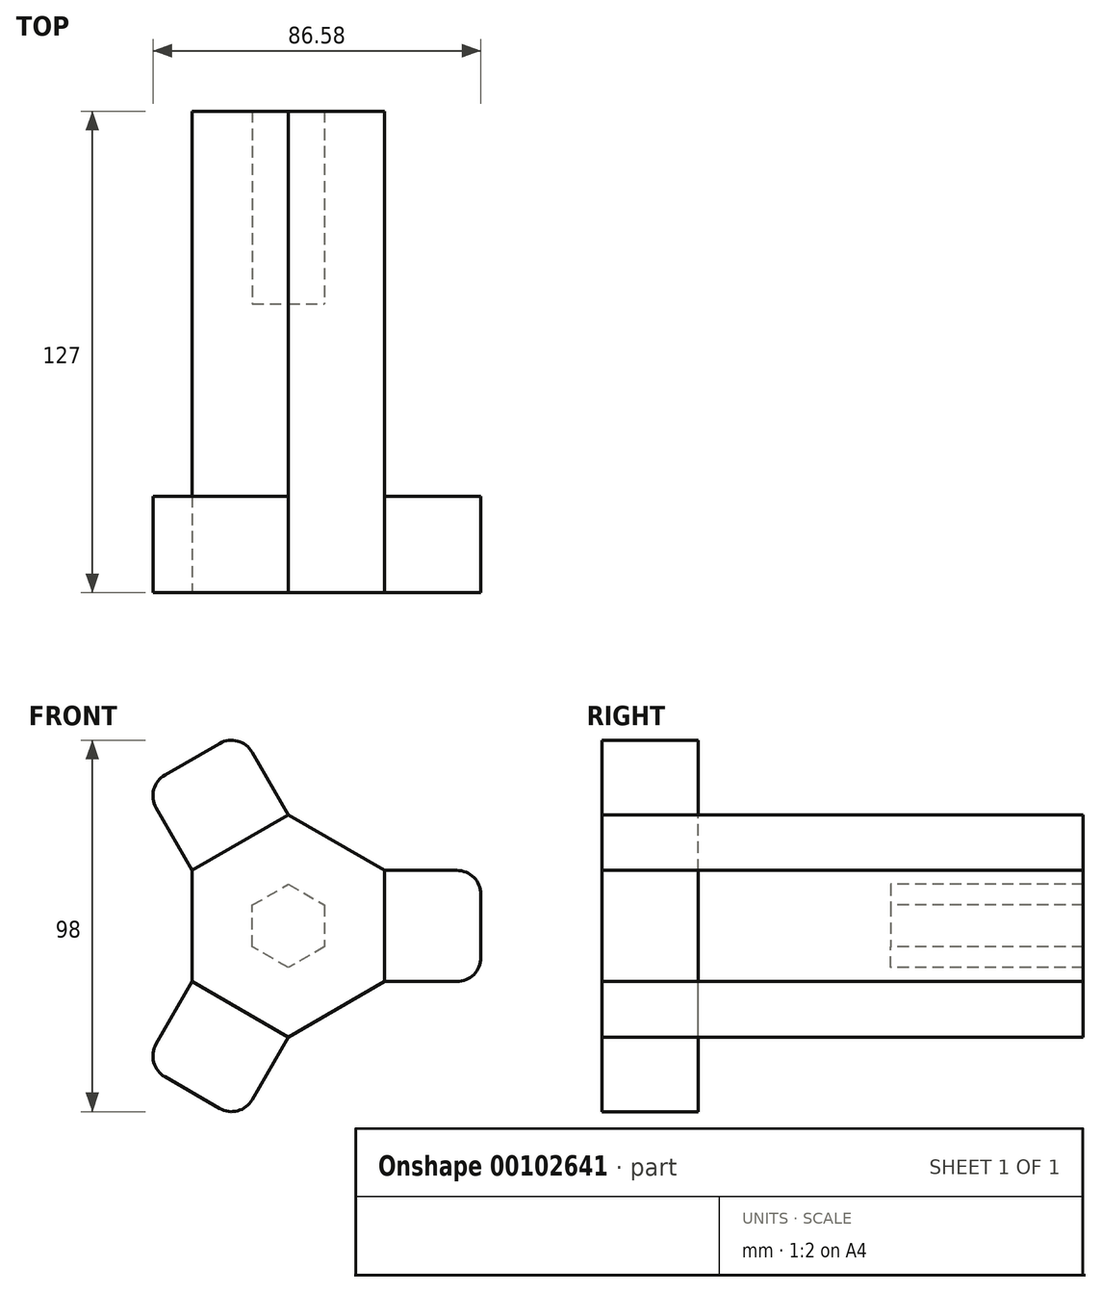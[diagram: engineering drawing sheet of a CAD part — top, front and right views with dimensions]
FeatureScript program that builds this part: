
annotation { "Feature Type Name" : "Feature", "Feature Type Description" : "" }
export const myFeature = defineFeature(function(context is Context, id is Id, definition is map)
    precondition{}
    {
        {
            var Q0;
            Q0=qCreatedBy(makeId("Front.planeOp"),FACE);
            var sketch = newSketch(context, id + "F0", { "sketchPlane" : qUnion([Q0])});
            skCircle(sketch, "E0.cCircle", {"center": v(-43.46, 32.73) * mm, "radius": 9.53 * mm, "construction": true});
            skLineSegment(sketch, "E0.0", {"start": v(-33.94, 38.23) * mm, "end": v(-33.94, 27.23) * mm});
            skLineSegment(sketch, "E0.1", {"start": v(-33.94, 27.23) * mm, "end": v(-43.46, 21.73) * mm});
            skLineSegment(sketch, "E0.2", {"start": v(-43.46, 21.73) * mm, "end": v(-52.99, 27.23) * mm});
            skLineSegment(sketch, "E0.3", {"start": v(-52.99, 27.23) * mm, "end": v(-52.99, 38.23) * mm});
            skLineSegment(sketch, "E0.4", {"start": v(-52.99, 38.23) * mm, "end": v(-43.46, 43.73) * mm});
            skLineSegment(sketch, "E0.5", {"start": v(-43.46, 43.73) * mm, "end": v(-33.94, 38.23) * mm});
            skPoint(sketch, "E0.0.midPoint", {"position": v(-33.94, 32.73) * mm});
            skCircle(sketch, "E1.cCircle", {"center": v(-43.46, 32.73) * mm, "radius": 25.4 * mm, "construction": true});
            skLineSegment(sketch, "E1.0", {"start": v(-18.06, 47.4) * mm, "end": v(-18.06, 18.07) * mm});
            skLineSegment(sketch, "E1.1", {"start": v(-18.06, 18.07) * mm, "end": v(-43.46, 3.4) * mm});
            skLineSegment(sketch, "E1.2", {"start": v(-43.46, 3.4) * mm, "end": v(-68.86, 18.07) * mm});
            skLineSegment(sketch, "E1.3", {"start": v(-68.86, 18.07) * mm, "end": v(-68.86, 47.4) * mm});
            skLineSegment(sketch, "E1.4", {"start": v(-68.86, 47.4) * mm, "end": v(-43.46, 62.06) * mm});
            skLineSegment(sketch, "E1.5", {"start": v(-43.46, 62.06) * mm, "end": v(-18.06, 47.4) * mm});
            skPoint(sketch, "E1.0.midPoint", {"position": v(-18.06, 32.73) * mm});
            skLineSegment(sketch, "E2", {"start": v(-18.06, 47.4) * mm, "end": v(0.99, 47.4) * mm});
            skLineSegment(sketch, "E3", {"start": v(7.34, 41.05) * mm, "end": v(7.34, 24.42) * mm});
            skLineSegment(sketch, "E4", {"start": v(0.99, 18.07) * mm, "end": v(-18.06, 18.07) * mm});
            skLineSegment(sketch, "E5.1.0", {"start": v(-68.86, 47.4) * mm, "end": v(-78.39, 63.9) * mm});
            skLineSegment(sketch, "E5.1.1", {"start": v(-76.06, 72.57) * mm, "end": v(-61.66, 80.88) * mm});
            skLineSegment(sketch, "E5.1.2", {"start": v(-52.99, 78.56) * mm, "end": v(-43.46, 62.06) * mm});
            skLineSegment(sketch, "E5.2.0", {"start": v(-43.46, 3.4) * mm, "end": v(-52.99, -13.1) * mm});
            skLineSegment(sketch, "E5.2.1", {"start": v(-61.66, -15.42) * mm, "end": v(-76.06, -7.1) * mm});
            skLineSegment(sketch, "E5.2.2", {"start": v(-78.39, 1.57) * mm, "end": v(-68.86, 18.07) * mm});
            skPoint(sketch, "E6.visualSharp", {"position": v(-81.56, 69.4) * mm});
            skArc(sketch, "E6.filletArc", {"start": v(-76.06, 72.57) * mm, "mid": v(-79.02, 68.71) * mm, "end": v(-78.39, 63.9) * mm});
            skPoint(sketch, "E7.visualSharp", {"position": v(-56.16, 84.06) * mm});
            skArc(sketch, "E7.filletArc", {"start": v(-52.99, 78.56) * mm, "mid": v(-56.84, 81.52) * mm, "end": v(-61.66, 80.88) * mm});
            skPoint(sketch, "E8.visualSharp", {"position": v(7.34, 47.4) * mm});
            skArc(sketch, "E8.filletArc", {"start": v(7.34, 41.05) * mm, "mid": v(5.48, 45.54) * mm, "end": v(0.99, 47.4) * mm});
            skPoint(sketch, "E9.visualSharp", {"position": v(-56.16, -18.6) * mm});
            skArc(sketch, "E9.filletArc", {"start": v(-61.66, -15.42) * mm, "mid": v(-56.84, -16.05) * mm, "end": v(-52.99, -13.1) * mm});
            skPoint(sketch, "E10.visualSharp", {"position": v(-81.56, -3.93) * mm});
            skArc(sketch, "E10.filletArc", {"start": v(-78.39, 1.57) * mm, "mid": v(-79.02, -3.25) * mm, "end": v(-76.06, -7.1) * mm});
            skPoint(sketch, "E11.visualSharp", {"position": v(7.34, 18.07) * mm});
            skArc(sketch, "E11.filletArc", {"start": v(0.99, 18.07) * mm, "mid": v(5.48, 19.93) * mm, "end": v(7.34, 24.42) * mm});
            skSolve(sketch);
        }
        {
            var Q0;
            Q0=makeQuery(id+"F0.imprint","IMPRINT",FACE,{"disambiguationData":[TD([[makeQuery(id+"F0.imprint","IMPRINT",EDGE,{"derivedFrom":sQuery(id+"F0.wireOp",EDGE,"E0.0")}),-1.0]])]});
            extrude(context, id + "F1", {"entities" : qUnion([Q0]), "oppositeDirection" : true, "depth" : 76.2 * mm});
        }
        {
            var Q0;
            Q0=makeQuery(id+"F0.imprint","IMPRINT",FACE,{"disambiguationData":[TD([[makeQuery(id+"F0.imprint","IMPRINT",EDGE,{"derivedFrom":sQuery(id+"F0.wireOp",EDGE,"E0.0")}),1.0]])]});
            extrude(context, id + "F2", {"entities" : qUnion([Q0]), "operationType" : NewBodyOperationType.ADD, "oppositeDirection" : true, "depth" : 127 * mm});
        }
        {
            var Q0;
            Q0=makeQuery(id+"F0.imprint","IMPRINT",FACE,{"disambiguationData":[TD([[makeQuery(id+"F0.imprint","IMPRINT",EDGE,{"derivedFrom":sQuery(id+"F0.wireOp",EDGE,"E1.4")}),1.0]])]});
            var Q1;
            Q1=makeQuery(id+"F0.imprint","IMPRINT",FACE,{"disambiguationData":[TD([[makeQuery(id+"F0.imprint","IMPRINT",EDGE,{"derivedFrom":sQuery(id+"F0.wireOp",EDGE,"E1.2")}),1.0]])]});
            var Q2;
            Q2=makeQuery(id+"F0.imprint","IMPRINT",FACE,{"disambiguationData":[TD([[makeQuery(id+"F0.imprint","IMPRINT",EDGE,{"derivedFrom":sQuery(id+"F0.wireOp",EDGE,"E1.0")}),1.0]])]});
            extrude(context, id + "F3", {"entities" : qUnion([Q0, Q1, Q2]), "oppositeDirection" : true, "depth" : 25.4 * mm});
        }
    });
